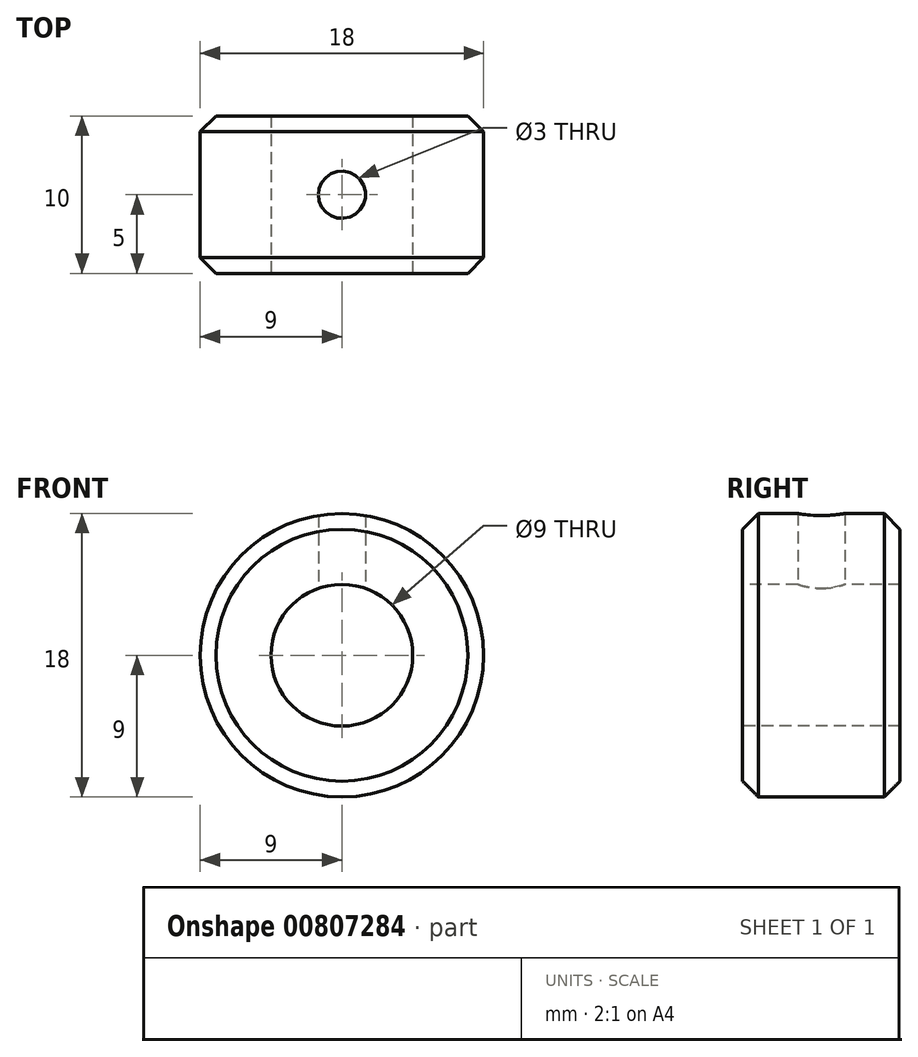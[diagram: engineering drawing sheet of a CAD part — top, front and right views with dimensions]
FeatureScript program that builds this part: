
annotation { "Feature Type Name" : "Feature", "Feature Type Description" : "" }
export const myFeature = defineFeature(function(context is Context, id is Id, definition is map)
    precondition{}
    {
        {
            var Q0;
            Q0=qCreatedBy(makeId("Front.planeOp"),FACE);
            var sketch = newSketch(context, id + "F0", { "sketchPlane" : qUnion([Q0])});
            skCircle(sketch, "E0", {"center": v(0, 0) * mm, "radius": 9 * mm});
            skCircle(sketch, "E1", {"center": v(0, 0) * mm, "radius": 4.5 * mm});
            skSolve(sketch);
        }
        {
            var Q0;
            Q0 = qSketchRegion(id + "F0", true);
            extrude(context, id + "F1", {"entities" : qUnion([Q0]), "oppositeDirection" : true, "depth" : 10 * mm, "offsetDistance" : 25 * mm, "symmetric" : true});
        }
        {
            var Q0;
            Q0=qCreatedBy(makeId("Top.planeOp"),FACE);
            var sketch = newSketch(context, id + "F2", { "sketchPlane" : qUnion([Q0])});
            skCircle(sketch, "E2", {"center": v(0, 0) * mm, "radius": 1.5 * mm});
            skSolve(sketch);
        }
        {
            var Q0;
            Q0 = qSketchRegion(id + "F2", true);
            extrude(context, id + "F3", {"entities" : qUnion([Q0]), "operationType" : NewBodyOperationType.REMOVE, "endBound" : BoundingType.THROUGH_ALL, "depth" : 25 * mm, "offsetDistance" : 25 * mm});
        }
        {
            var Q0;
            Q0=makeQuery(id+"F1.opExtrude","CAP_EDGE",EDGE,{"disambiguationData":[OSD([sQuery(id+"F0.wireOp",EDGE,"E0")])],"isStart":true});
            var Q1;
            Q1=makeQuery(id+"F1.opExtrude","CAP_EDGE",EDGE,{"disambiguationData":[OSD([sQuery(id+"F0.wireOp",EDGE,"E0")])],"isStart":false});
            chamfer(context, id + "F4", {"entities" : qUnion([Q0, Q1]), "width" : 1 * mm, "tangentPropagation" : true});
        }
    });
